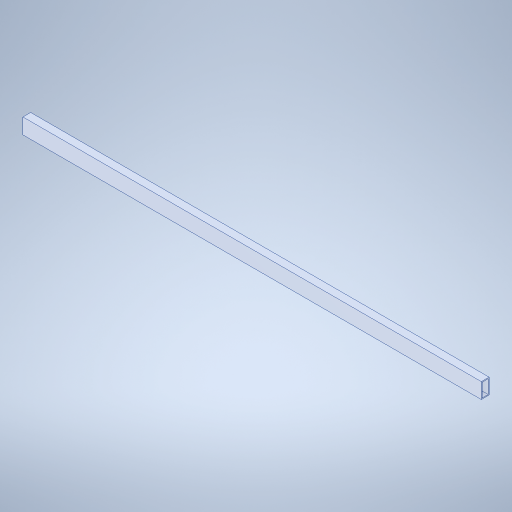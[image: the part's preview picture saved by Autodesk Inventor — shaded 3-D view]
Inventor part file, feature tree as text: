
AUTODESK INVENTOR PART (.ipt)
format: ipt  version: 2023.4 (Build 274418000, 418)  size: 247,808 bytes
history: native  units: in
note: dims shown in document units (in); Inventor stores cm internally (conversion verified against a paired STEP export)
features: extrude x1
ambient origin geometry x8: Origin, YZ Plane, XZ Plane, XY Plane, X Axis, Y Axis, Z Axis, Center Point
bodies: Solid1 (feature_tree)
feature tree (1):
  extrude  "Extrude-Thin1"  [1 undecoded]
note: 1 required parameter value undecoded (feature->parameter linkage not recoverable at this tier; creation-order binding heuristic only, values carry confidence <= 0.55)
